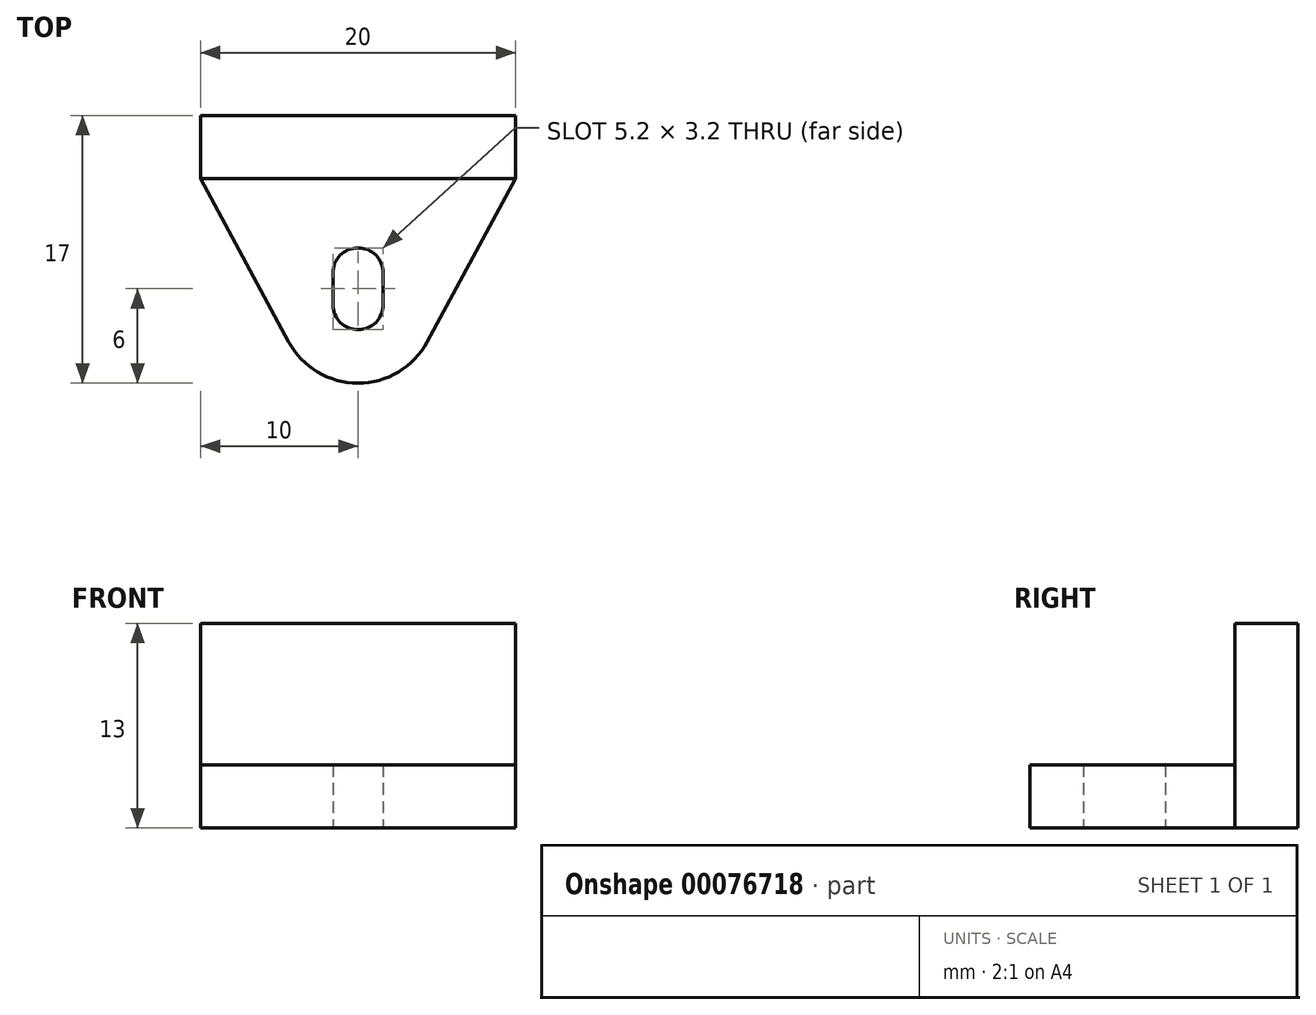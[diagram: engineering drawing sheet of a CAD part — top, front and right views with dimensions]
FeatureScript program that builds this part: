
annotation { "Feature Type Name" : "Feature", "Feature Type Description" : "" }
export const myFeature = defineFeature(function(context is Context, id is Id, definition is map)
    precondition{}
    {
        {
            var Q0;
            Q0=qCreatedBy(makeId("Top.planeOp"),FACE);
            var sketch = newSketch(context, id + "F0", { "sketchPlane" : qUnion([Q0])});
            skLineSegment(sketch, "E0.bottom", {"start": v(10, -2) * mm, "end": v(-10, -2) * mm});
            skLineSegment(sketch, "E0.top", {"start": v(10, 2) * mm, "end": v(-10, 2) * mm});
            skLineSegment(sketch, "E0.left", {"start": v(10, -2) * mm, "end": v(10, 2) * mm});
            skLineSegment(sketch, "E0.right", {"start": v(-10, -2) * mm, "end": v(-10, 2) * mm});
            skPoint(sketch, "E0.middle", {"position": v(0, 0) * mm});
            skLineSegment(sketch, "E1", {"start": v(0, -2) * mm, "end": v(0, -8) * mm, "construction": true});
            skLineSegment(sketch, "E2", {"start": v(0, -8) * mm, "end": v(0, -10) * mm, "construction": true});
            skArc(sketch, "E3.0.startCap", {"start": v(-1.6, -8) * mm, "mid": v(0, -6.4) * mm, "end": v(1.6, -8) * mm});
            skArc(sketch, "E3.0.endCap", {"start": v(1.6, -10) * mm, "mid": v(0, -11.6) * mm, "end": v(-1.6, -10) * mm});
            skLineSegment(sketch, "E3.0.left", {"start": v(1.6, -8) * mm, "end": v(1.6, -10) * mm});
            skLineSegment(sketch, "E3.0.right", {"start": v(-1.6, -8) * mm, "end": v(-1.6, -10) * mm});
            skArc(sketch, "E4", {"start": v(-4.4, -12.37) * mm, "mid": v(0, -15) * mm, "end": v(4.4, -12.37) * mm});
            skLineSegment(sketch, "E5", {"start": v(-10, -2) * mm, "end": v(-4.4, -12.37) * mm});
            skLineSegment(sketch, "E6", {"start": v(10, -2) * mm, "end": v(4.4, -12.37) * mm});
            skSolve(sketch);
        }
        {
            var Q0;
            Q0=makeQuery(id+"F0.imprint","IMPRINT",FACE,{"disambiguationData":[TD([[makeQuery(id+"F0.imprint","IMPRINT",EDGE,{"derivedFrom":sQuery(id+"F0.wireOp",EDGE,"E0.bottom")}),1.0]])]});
            extrude(context, id + "F1", {"entities" : qUnion([Q0]), "depth" : 4 * mm});
        }
        {
            var Q0;
            Q0=makeQuery(id+"F0.imprint","IMPRINT",FACE,{"disambiguationData":[TD([[makeQuery(id+"F0.imprint","IMPRINT",EDGE,{"derivedFrom":sQuery(id+"F0.wireOp",EDGE,"E0.bottom")}),-1.0]])]});
            extrude(context, id + "F2", {"entities" : qUnion([Q0]), "operationType" : NewBodyOperationType.ADD, "depth" : 13 * mm});
        }
    });
